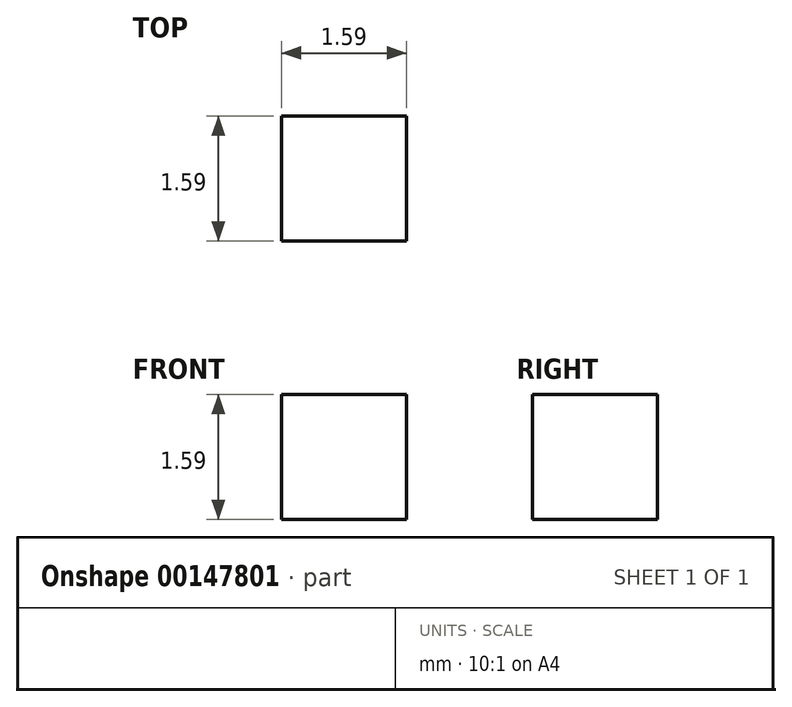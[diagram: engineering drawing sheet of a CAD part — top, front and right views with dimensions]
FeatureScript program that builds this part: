
annotation { "Feature Type Name" : "Feature", "Feature Type Description" : "" }
export const myFeature = defineFeature(function(context is Context, id is Id, definition is map)
    precondition{}
    {
        {
            var Q0;
            Q0=qCreatedBy(makeId("Top.planeOp"),FACE);
            var sketch = newSketch(context, id + "F0", { "sketchPlane" : qUnion([Q0])});
            skLineSegment(sketch, "E0.bottom", {"start": v(0, 0) * mm, "end": v(-1.59, 0) * mm});
            skLineSegment(sketch, "E0.top", {"start": v(0, -1.59) * mm, "end": v(-1.59, -1.59) * mm});
            skLineSegment(sketch, "E0.left", {"start": v(0, 0) * mm, "end": v(0, -1.59) * mm});
            skLineSegment(sketch, "E0.right", {"start": v(-1.59, 0) * mm, "end": v(-1.59, -1.59) * mm});
            skSolve(sketch);
        }
        {
            var Q0;
            Q0=qSketchRegion(id+"F0",true);
            extrude(context, id + "F1", {"entities" : qUnion([Q0]), "depth" : 1.59 * mm});
        }
    });
